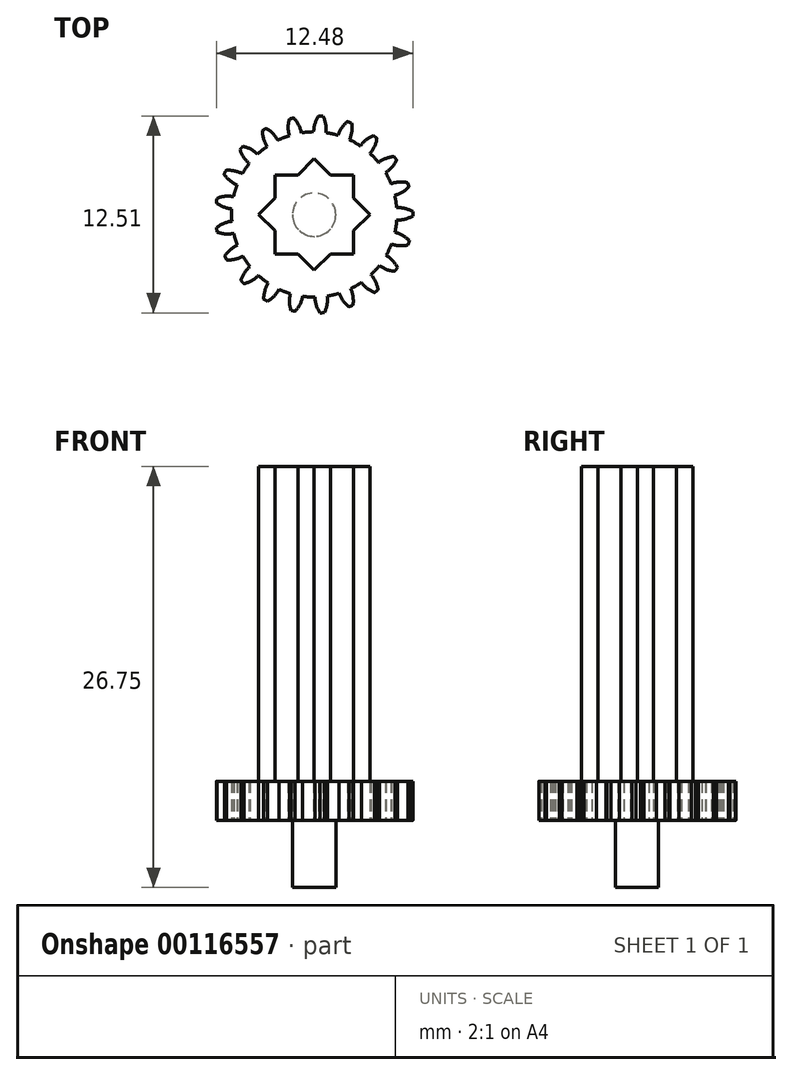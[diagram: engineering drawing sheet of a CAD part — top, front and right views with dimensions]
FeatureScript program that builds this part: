
annotation { "Feature Type Name" : "Feature", "Feature Type Description" : "" }
export const myFeature = defineFeature(function(context is Context, id is Id, definition is map)
    precondition{}
    {
        {
            var Q0;
            Q0=qCreatedBy(makeId("Top.planeOp"),FACE);
            var sketch = newSketch(context, id + "F0", { "sketchPlane" : qUnion([Q0])});
            skLineSegment(sketch, "E0", {"start": v(61.42, 3.14) * mm, "end": v(65.52, 3.14) * mm, "construction": true});
            skLineSegment(sketch, "E1", {"start": v(61.42, 3.14) * mm, "end": v(65.31, 4.4) * mm, "construction": true});
            skLineSegment(sketch, "E2", {"start": v(61.42, 3.14) * mm, "end": v(65.72, 3.82) * mm, "construction": true});
            skPoint(sketch, "E3.third.point", {"position": v(57.79, 0) * mm});
            skArc(sketch, "E4.MirrorCS", {"start": v(62.86, 3.22) * mm, "mid": v(63.38, 3.1) * mm, "end": v(63.92, 3.14) * mm});
            skArc(sketch, "E5.MirrorCS", {"start": v(62.86, 3.22) * mm, "mid": v(62.85, 3.3) * mm, "end": v(62.84, 3.36) * mm});
            skArc(sketch, "E6.MirrorCS", {"start": v(62.82, 3.5) * mm, "mid": v(62.83, 3.43) * mm, "end": v(62.84, 3.36) * mm});
            skArc(sketch, "E7.MirrorCS", {"start": v(62.82, 3.5) * mm, "mid": v(63.28, 3.78) * mm, "end": v(63.8, 3.9) * mm});
            skLineSegment(sketch, "E8", {"start": v(69.03, 4.34) * mm, "end": v(63.8, 3.9) * mm, "construction": true});
            skArc(sketch, "E9.1.0", {"start": v(63.34, 1.7) * mm, "mid": v(63.7, 2.1) * mm, "end": v(64.15, 2.39) * mm});
            skArc(sketch, "E9.1.1", {"start": v(63.34, 1.7) * mm, "mid": v(63.37, 1.64) * mm, "end": v(63.4, 1.58) * mm});
            skArc(sketch, "E9.1.2", {"start": v(63.46, 1.46) * mm, "mid": v(63.43, 1.52) * mm, "end": v(63.4, 1.58) * mm});
            skArc(sketch, "E9.1.3", {"start": v(63.46, 1.46) * mm, "mid": v(64, 1.5) * mm, "end": v(64.5, 1.68) * mm});
            skArc(sketch, "E9.2.0", {"start": v(64.37, 0.15) * mm, "mid": v(64.6, 0.63) * mm, "end": v(64.95, 1.04) * mm});
            skArc(sketch, "E9.2.1", {"start": v(64.37, 0.15) * mm, "mid": v(64.42, 0.1) * mm, "end": v(64.46, 0.05) * mm});
            skArc(sketch, "E9.2.2", {"start": v(64.56, -0.05) * mm, "mid": v(64.51, 0) * mm, "end": v(64.46, 0.05) * mm});
            skArc(sketch, "E9.2.3", {"start": v(64.56, -0.05) * mm, "mid": v(65.06, 0.14) * mm, "end": v(65.48, 0.47) * mm});
            skArc(sketch, "E9.3.0", {"start": v(65.81, -1.04) * mm, "mid": v(65.88, -0.5) * mm, "end": v(66.1, -0.02) * mm});
            skArc(sketch, "E9.3.1", {"start": v(65.81, -1.04) * mm, "mid": v(65.87, -1.07) * mm, "end": v(65.93, -1.1) * mm});
            skArc(sketch, "E9.3.2", {"start": v(66.06, -1.17) * mm, "mid": v(66, -1.14) * mm, "end": v(65.93, -1.1) * mm});
            skArc(sketch, "E9.3.3", {"start": v(66.06, -1.17) * mm, "mid": v(66.47, -0.84) * mm, "end": v(66.78, -0.4) * mm});
            skArc(sketch, "E9.4.0", {"start": v(67.54, -1.74) * mm, "mid": v(67.45, -1.22) * mm, "end": v(67.52, -0.69) * mm});
            skArc(sketch, "E9.4.1", {"start": v(67.54, -1.74) * mm, "mid": v(67.6, -1.76) * mm, "end": v(67.68, -1.78) * mm});
            skArc(sketch, "E9.4.2", {"start": v(67.81, -1.8) * mm, "mid": v(67.75, -1.8) * mm, "end": v(67.68, -1.78) * mm});
            skArc(sketch, "E9.4.3", {"start": v(67.81, -1.8) * mm, "mid": v(68.12, -1.36) * mm, "end": v(68.28, -0.85) * mm});
            skArc(sketch, "E9.5.0", {"start": v(69.4, -1.91) * mm, "mid": v(69.16, -1.43) * mm, "end": v(69.07, -0.9) * mm});
            skArc(sketch, "E9.5.1", {"start": v(69.4, -1.91) * mm, "mid": v(69.47, -1.9) * mm, "end": v(69.54, -1.9) * mm});
            skArc(sketch, "E9.5.2", {"start": v(69.68, -1.89) * mm, "mid": v(69.61, -1.9) * mm, "end": v(69.54, -1.9) * mm});
            skArc(sketch, "E9.5.3", {"start": v(69.68, -1.89) * mm, "mid": v(69.84, -1.38) * mm, "end": v(69.85, -0.84) * mm});
            skArc(sketch, "E9.6.0", {"start": v(71.23, -1.52) * mm, "mid": v(70.86, -1.14) * mm, "end": v(70.61, -0.66) * mm});
            skArc(sketch, "E9.6.1", {"start": v(71.23, -1.52) * mm, "mid": v(71.3, -1.5) * mm, "end": v(71.36, -1.47) * mm});
            skArc(sketch, "E9.6.2", {"start": v(71.49, -1.42) * mm, "mid": v(71.42, -1.45) * mm, "end": v(71.36, -1.47) * mm});
            skArc(sketch, "E9.6.3", {"start": v(71.49, -1.42) * mm, "mid": v(71.49, -0.88) * mm, "end": v(71.34, -0.37) * mm});
            skArc(sketch, "E9.7.0", {"start": v(72.86, -0.61) * mm, "mid": v(72.4, -0.35) * mm, "end": v(72.02, 0.03) * mm});
            skArc(sketch, "E9.7.1", {"start": v(72.86, -0.61) * mm, "mid": v(72.91, -0.57) * mm, "end": v(72.97, -0.53) * mm});
            skArc(sketch, "E9.7.2", {"start": v(73.08, -0.44) * mm, "mid": v(73.02, -0.48) * mm, "end": v(72.97, -0.53) * mm});
            skArc(sketch, "E9.7.3", {"start": v(73.08, -0.44) * mm, "mid": v(72.92, 0.07) * mm, "end": v(72.62, 0.52) * mm});
            skArc(sketch, "E9.8.0", {"start": v(74.15, 0.74) * mm, "mid": v(73.63, 0.85) * mm, "end": v(73.16, 1.1) * mm});
            skArc(sketch, "E9.8.1", {"start": v(74.15, 0.74) * mm, "mid": v(74.19, 0.8) * mm, "end": v(74.23, 0.85) * mm});
            skArc(sketch, "E9.8.2", {"start": v(74.3, 0.97) * mm, "mid": v(74.27, 0.9) * mm, "end": v(74.23, 0.85) * mm});
            skArc(sketch, "E9.8.3", {"start": v(74.3, 0.97) * mm, "mid": v(74, 1.41) * mm, "end": v(73.6, 1.75) * mm});
            skArc(sketch, "E9.9.0", {"start": v(74.98, 2.4) * mm, "mid": v(74.45, 2.36) * mm, "end": v(73.93, 2.46) * mm});
            skArc(sketch, "E9.9.1", {"start": v(74.98, 2.4) * mm, "mid": v(75, 2.47) * mm, "end": v(75.03, 2.54) * mm});
            skArc(sketch, "E9.9.2", {"start": v(75.06, 2.67) * mm, "mid": v(75.05, 2.6) * mm, "end": v(75.03, 2.54) * mm});
            skArc(sketch, "E9.9.3", {"start": v(75.06, 2.67) * mm, "mid": v(74.65, 3) * mm, "end": v(74.15, 3.21) * mm});
            skArc(sketch, "E9.10.0", {"start": v(75.29, 4.25) * mm, "mid": v(74.8, 4.05) * mm, "end": v(74.26, 4) * mm});
            skArc(sketch, "E9.10.1", {"start": v(75.29, 4.25) * mm, "mid": v(75.3, 4.32) * mm, "end": v(75.3, 4.39) * mm});
            skArc(sketch, "E9.10.2", {"start": v(75.29, 4.53) * mm, "mid": v(75.3, 4.46) * mm, "end": v(75.3, 4.39) * mm});
            skArc(sketch, "E9.10.3", {"start": v(75.29, 4.53) * mm, "mid": v(74.8, 4.72) * mm, "end": v(74.26, 4.77) * mm});
            skArc(sketch, "E9.11.0", {"start": v(75.04, 6.1) * mm, "mid": v(74.63, 5.76) * mm, "end": v(74.13, 5.55) * mm});
            skArc(sketch, "E9.11.1", {"start": v(75.04, 6.1) * mm, "mid": v(75.02, 6.17) * mm, "end": v(75, 6.23) * mm});
            skArc(sketch, "E9.11.2", {"start": v(74.95, 6.37) * mm, "mid": v(74.98, 6.3) * mm, "end": v(75, 6.23) * mm});
            skArc(sketch, "E9.11.3", {"start": v(74.95, 6.37) * mm, "mid": v(74.42, 6.4) * mm, "end": v(73.9, 6.3) * mm});
            skArc(sketch, "E9.12.0", {"start": v(74.25, 7.8) * mm, "mid": v(73.96, 7.35) * mm, "end": v(73.55, 7) * mm});
            skArc(sketch, "E9.12.1", {"start": v(74.25, 7.8) * mm, "mid": v(74.22, 7.85) * mm, "end": v(74.18, 7.91) * mm});
            skArc(sketch, "E9.12.2", {"start": v(74.1, 8.02) * mm, "mid": v(74.14, 7.97) * mm, "end": v(74.18, 7.91) * mm});
            skArc(sketch, "E9.12.3", {"start": v(74.1, 8.02) * mm, "mid": v(73.57, 7.9) * mm, "end": v(73.1, 7.65) * mm});
            skArc(sketch, "E9.13.0", {"start": v(73, 9.18) * mm, "mid": v(72.85, 8.67) * mm, "end": v(72.57, 8.22) * mm});
            skArc(sketch, "E9.13.1", {"start": v(73, 9.18) * mm, "mid": v(72.95, 9.23) * mm, "end": v(72.9, 9.27) * mm});
            skArc(sketch, "E9.13.2", {"start": v(72.78, 9.35) * mm, "mid": v(72.84, 9.31) * mm, "end": v(72.9, 9.27) * mm});
            skArc(sketch, "E9.13.3", {"start": v(72.78, 9.35) * mm, "mid": v(72.32, 9.09) * mm, "end": v(71.95, 8.7) * mm});
            skArc(sketch, "E9.14.0", {"start": v(71.4, 10.14) * mm, "mid": v(71.4, 9.6) * mm, "end": v(71.27, 9.09) * mm});
            skArc(sketch, "E9.14.1", {"start": v(71.4, 10.14) * mm, "mid": v(71.34, 10.17) * mm, "end": v(71.27, 10.2) * mm});
            skArc(sketch, "E9.14.2", {"start": v(71.14, 10.24) * mm, "mid": v(71.2, 10.22) * mm, "end": v(71.27, 10.2) * mm});
            skArc(sketch, "E9.14.3", {"start": v(71.14, 10.24) * mm, "mid": v(70.78, 9.85) * mm, "end": v(70.54, 9.37) * mm});
            skArc(sketch, "E9.15.0", {"start": v(69.59, 10.58) * mm, "mid": v(69.75, 10.07) * mm, "end": v(69.77, 9.54) * mm});
            skArc(sketch, "E9.15.1", {"start": v(69.59, 10.58) * mm, "mid": v(69.52, 10.59) * mm, "end": v(69.45, 10.6) * mm});
            skArc(sketch, "E9.15.2", {"start": v(69.3, 10.6) * mm, "mid": v(69.38, 10.6) * mm, "end": v(69.45, 10.6) * mm});
            skArc(sketch, "E9.15.3", {"start": v(69.3, 10.6) * mm, "mid": v(69.07, 10.12) * mm, "end": v(68.99, 9.6) * mm});
            skArc(sketch, "E9.16.0", {"start": v(67.72, 10.47) * mm, "mid": v(68.03, 10.03) * mm, "end": v(68.2, 9.53) * mm});
            skArc(sketch, "E9.16.1", {"start": v(67.72, 10.47) * mm, "mid": v(67.65, 10.46) * mm, "end": v(67.59, 10.44) * mm});
            skArc(sketch, "E9.16.2", {"start": v(67.45, 10.4) * mm, "mid": v(67.52, 10.42) * mm, "end": v(67.59, 10.44) * mm});
            skArc(sketch, "E9.16.3", {"start": v(67.45, 10.4) * mm, "mid": v(67.37, 9.88) * mm, "end": v(67.44, 9.35) * mm});
            skArc(sketch, "E9.17.0", {"start": v(65.97, 9.81) * mm, "mid": v(66.4, 9.49) * mm, "end": v(66.71, 9.05) * mm});
            skArc(sketch, "E9.17.1", {"start": v(65.97, 9.81) * mm, "mid": v(65.91, 9.78) * mm, "end": v(65.85, 9.75) * mm});
            skArc(sketch, "E9.17.2", {"start": v(65.73, 9.67) * mm, "mid": v(65.8, 9.7) * mm, "end": v(65.85, 9.75) * mm});
            skArc(sketch, "E9.17.3", {"start": v(65.73, 9.67) * mm, "mid": v(65.81, 9.14) * mm, "end": v(66.04, 8.66) * mm});
            skArc(sketch, "E9.18.0", {"start": v(64.5, 8.67) * mm, "mid": v(65, 8.48) * mm, "end": v(65.43, 8.16) * mm});
            skArc(sketch, "E9.18.1", {"start": v(64.5, 8.67) * mm, "mid": v(64.45, 8.62) * mm, "end": v(64.4, 8.57) * mm});
            skArc(sketch, "E9.18.2", {"start": v(64.3, 8.47) * mm, "mid": v(64.35, 8.52) * mm, "end": v(64.4, 8.57) * mm});
            skArc(sketch, "E9.18.3", {"start": v(64.3, 8.47) * mm, "mid": v(64.54, 7.98) * mm, "end": v(64.9, 7.59) * mm});
            skArc(sketch, "E9.19.0", {"start": v(63.42, 7.14) * mm, "mid": v(63.96, 7.11) * mm, "end": v(64.46, 6.93) * mm});
            skArc(sketch, "E9.19.1", {"start": v(63.42, 7.14) * mm, "mid": v(63.4, 7.08) * mm, "end": v(63.36, 7.02) * mm});
            skArc(sketch, "E9.19.2", {"start": v(63.3, 6.9) * mm, "mid": v(63.33, 6.96) * mm, "end": v(63.36, 7.02) * mm});
            skArc(sketch, "E9.19.3", {"start": v(63.3, 6.9) * mm, "mid": v(63.67, 6.5) * mm, "end": v(64.12, 6.22) * mm});
            skArc(sketch, "E9.20.0", {"start": v(62.85, 5.37) * mm, "mid": v(63.36, 5.5) * mm, "end": v(63.9, 5.47) * mm});
            skArc(sketch, "E9.20.1", {"start": v(62.85, 5.37) * mm, "mid": v(62.83, 5.3) * mm, "end": v(62.82, 5.23) * mm});
            skArc(sketch, "E9.20.2", {"start": v(62.8, 5.1) * mm, "mid": v(62.81, 5.16) * mm, "end": v(62.82, 5.23) * mm});
            skArc(sketch, "E9.20.3", {"start": v(62.8, 5.1) * mm, "mid": v(63.27, 4.82) * mm, "end": v(63.79, 4.7) * mm});
            skPoint(sketch, "E9.center", {"position": v(69.03, 4.34) * mm});
            skCircle(sketch, "E10", {"center": v(69.03, 4.34) * mm, "radius": 5.25 * mm});
            skSolve(sketch);
        }
        {
            var Q0;
            Q0=qSketchRegion(id+"F0",true);
            extrude(context, id + "F1", {"entities" : qUnion([Q0]), "depth" : 2.5 * mm});
        }
        {
            var Q0;
            Q0=makeQuery(id+"F1.opExtrude","CAP_FACE",FACE,{"disambiguationData":[OSD([sQuery(id+"F0.wireOp",EDGE,"E4.MirrorCS"),sQuery(id+"F0.wireOp",EDGE,"E5.MirrorCS"),sQuery(id+"F0.wireOp",EDGE,"E6.MirrorCS"),sQuery(id+"F0.wireOp",EDGE,"E7.MirrorCS"),sQuery(id+"F0.wireOp",EDGE,"3aad1c11-f46f-48f3-83f1-c81cc0587eb40.MirrorCS"),sQuery(id+"F0.wireOp",EDGE,"261d038e-785b-489d-9701-d77bc27e36f7.1.0"),sQuery(id+"F0.wireOp",EDGE,"261d038e-785b-489d-9701-d77bc27e36f7.1.1"),sQuery(id+"F0.wireOp",EDGE,"261d038e-785b-489d-9701-d77bc27e36f7.1.2"),sQuery(id+"F0.wireOp",EDGE,"261d038e-785b-489d-9701-d77bc27e36f7.1.3"),sQuery(id+"F0.wireOp",EDGE,"261d038e-785b-489d-9701-d77bc27e36f7.1.4"),sQuery(id+"F0.wireOp",EDGE,"261d038e-785b-489d-9701-d77bc27e36f7.2.0"),sQuery(id+"F0.wireOp",EDGE,"261d038e-785b-489d-9701-d77bc27e36f7.2.1"),sQuery(id+"F0.wireOp",EDGE,"261d038e-785b-489d-9701-d77bc27e36f7.2.2"),sQuery(id+"F0.wireOp",EDGE,"261d038e-785b-489d-9701-d77bc27e36f7.2.3"),sQuery(id+"F0.wireOp",EDGE,"261d038e-785b-489d-9701-d77bc27e36f7.2.4"),sQuery(id+"F0.wireOp",EDGE,"261d038e-785b-489d-9701-d77bc27e36f7.3.0"),sQuery(id+"F0.wireOp",EDGE,"261d038e-785b-489d-9701-d77bc27e36f7.3.1"),sQuery(id+"F0.wireOp",EDGE,"261d038e-785b-489d-9701-d77bc27e36f7.3.2"),sQuery(id+"F0.wireOp",EDGE,"261d038e-785b-489d-9701-d77bc27e36f7.3.3"),sQuery(id+"F0.wireOp",EDGE,"261d038e-785b-489d-9701-d77bc27e36f7.3.4"),sQuery(id+"F0.wireOp",EDGE,"261d038e-785b-489d-9701-d77bc27e36f7.4.0"),sQuery(id+"F0.wireOp",EDGE,"261d038e-785b-489d-9701-d77bc27e36f7.4.1"),sQuery(id+"F0.wireOp",EDGE,"261d038e-785b-489d-9701-d77bc27e36f7.4.2"),sQuery(id+"F0.wireOp",EDGE,"261d038e-785b-489d-9701-d77bc27e36f7.4.3"),sQuery(id+"F0.wireOp",EDGE,"261d038e-785b-489d-9701-d77bc27e36f7.4.4"),sQuery(id+"F0.wireOp",EDGE,"261d038e-785b-489d-9701-d77bc27e36f7.5.0"),sQuery(id+"F0.wireOp",EDGE,"261d038e-785b-489d-9701-d77bc27e36f7.5.1"),sQuery(id+"F0.wireOp",EDGE,"261d038e-785b-489d-9701-d77bc27e36f7.5.2"),sQuery(id+"F0.wireOp",EDGE,"261d038e-785b-489d-9701-d77bc27e36f7.5.3"),sQuery(id+"F0.wireOp",EDGE,"261d038e-785b-489d-9701-d77bc27e36f7.5.4"),sQuery(id+"F0.wireOp",EDGE,"261d038e-785b-489d-9701-d77bc27e36f7.6.0"),sQuery(id+"F0.wireOp",EDGE,"261d038e-785b-489d-9701-d77bc27e36f7.6.1"),sQuery(id+"F0.wireOp",EDGE,"261d038e-785b-489d-9701-d77bc27e36f7.6.2"),sQuery(id+"F0.wireOp",EDGE,"261d038e-785b-489d-9701-d77bc27e36f7.6.3"),sQuery(id+"F0.wireOp",EDGE,"261d038e-785b-489d-9701-d77bc27e36f7.6.4"),sQuery(id+"F0.wireOp",EDGE,"261d038e-785b-489d-9701-d77bc27e36f7.7.0"),sQuery(id+"F0.wireOp",EDGE,"261d038e-785b-489d-9701-d77bc27e36f7.7.1"),sQuery(id+"F0.wireOp",EDGE,"261d038e-785b-489d-9701-d77bc27e36f7.7.2"),sQuery(id+"F0.wireOp",EDGE,"261d038e-785b-489d-9701-d77bc27e36f7.7.3"),sQuery(id+"F0.wireOp",EDGE,"261d038e-785b-489d-9701-d77bc27e36f7.7.4"),sQuery(id+"F0.wireOp",EDGE,"261d038e-785b-489d-9701-d77bc27e36f7.8.0"),sQuery(id+"F0.wireOp",EDGE,"261d038e-785b-489d-9701-d77bc27e36f7.8.1"),sQuery(id+"F0.wireOp",EDGE,"261d038e-785b-489d-9701-d77bc27e36f7.8.2"),sQuery(id+"F0.wireOp",EDGE,"261d038e-785b-489d-9701-d77bc27e36f7.8.3"),sQuery(id+"F0.wireOp",EDGE,"261d038e-785b-489d-9701-d77bc27e36f7.8.4"),sQuery(id+"F0.wireOp",EDGE,"261d038e-785b-489d-9701-d77bc27e36f7.9.0"),sQuery(id+"F0.wireOp",EDGE,"261d038e-785b-489d-9701-d77bc27e36f7.9.1"),sQuery(id+"F0.wireOp",EDGE,"261d038e-785b-489d-9701-d77bc27e36f7.9.2"),sQuery(id+"F0.wireOp",EDGE,"261d038e-785b-489d-9701-d77bc27e36f7.9.3"),sQuery(id+"F0.wireOp",EDGE,"261d038e-785b-489d-9701-d77bc27e36f7.9.4"),sQuery(id+"F0.wireOp",EDGE,"261d038e-785b-489d-9701-d77bc27e36f7.10.0"),sQuery(id+"F0.wireOp",EDGE,"261d038e-785b-489d-9701-d77bc27e36f7.10.1"),sQuery(id+"F0.wireOp",EDGE,"261d038e-785b-489d-9701-d77bc27e36f7.10.2"),sQuery(id+"F0.wireOp",EDGE,"261d038e-785b-489d-9701-d77bc27e36f7.10.3"),sQuery(id+"F0.wireOp",EDGE,"261d038e-785b-489d-9701-d77bc27e36f7.10.4"),sQuery(id+"F0.wireOp",EDGE,"261d038e-785b-489d-9701-d77bc27e36f7.11.0"),sQuery(id+"F0.wireOp",EDGE,"261d038e-785b-489d-9701-d77bc27e36f7.11.1"),sQuery(id+"F0.wireOp",EDGE,"261d038e-785b-489d-9701-d77bc27e36f7.11.2"),sQuery(id+"F0.wireOp",EDGE,"261d038e-785b-489d-9701-d77bc27e36f7.11.3"),sQuery(id+"F0.wireOp",EDGE,"261d038e-785b-489d-9701-d77bc27e36f7.11.4"),sQuery(id+"F0.wireOp",EDGE,"261d038e-785b-489d-9701-d77bc27e36f7.12.0"),sQuery(id+"F0.wireOp",EDGE,"261d038e-785b-489d-9701-d77bc27e36f7.12.1"),sQuery(id+"F0.wireOp",EDGE,"261d038e-785b-489d-9701-d77bc27e36f7.12.2"),sQuery(id+"F0.wireOp",EDGE,"261d038e-785b-489d-9701-d77bc27e36f7.12.3"),sQuery(id+"F0.wireOp",EDGE,"261d038e-785b-489d-9701-d77bc27e36f7.12.4"),sQuery(id+"F0.wireOp",EDGE,"261d038e-785b-489d-9701-d77bc27e36f7.13.0"),sQuery(id+"F0.wireOp",EDGE,"261d038e-785b-489d-9701-d77bc27e36f7.13.1"),sQuery(id+"F0.wireOp",EDGE,"261d038e-785b-489d-9701-d77bc27e36f7.13.2"),sQuery(id+"F0.wireOp",EDGE,"261d038e-785b-489d-9701-d77bc27e36f7.13.3"),sQuery(id+"F0.wireOp",EDGE,"261d038e-785b-489d-9701-d77bc27e36f7.13.4"),sQuery(id+"F0.wireOp",EDGE,"261d038e-785b-489d-9701-d77bc27e36f7.14.0"),sQuery(id+"F0.wireOp",EDGE,"261d038e-785b-489d-9701-d77bc27e36f7.14.1"),sQuery(id+"F0.wireOp",EDGE,"261d038e-785b-489d-9701-d77bc27e36f7.14.2"),sQuery(id+"F0.wireOp",EDGE,"261d038e-785b-489d-9701-d77bc27e36f7.14.3"),sQuery(id+"F0.wireOp",EDGE,"261d038e-785b-489d-9701-d77bc27e36f7.14.4"),sQuery(id+"F0.wireOp",EDGE,"261d038e-785b-489d-9701-d77bc27e36f7.15.0"),sQuery(id+"F0.wireOp",EDGE,"261d038e-785b-489d-9701-d77bc27e36f7.15.1"),sQuery(id+"F0.wireOp",EDGE,"261d038e-785b-489d-9701-d77bc27e36f7.15.2"),sQuery(id+"F0.wireOp",EDGE,"261d038e-785b-489d-9701-d77bc27e36f7.15.3"),sQuery(id+"F0.wireOp",EDGE,"261d038e-785b-489d-9701-d77bc27e36f7.15.4"),sQuery(id+"F0.wireOp",EDGE,"261d038e-785b-489d-9701-d77bc27e36f7.16.0"),sQuery(id+"F0.wireOp",EDGE,"261d038e-785b-489d-9701-d77bc27e36f7.16.1"),sQuery(id+"F0.wireOp",EDGE,"261d038e-785b-489d-9701-d77bc27e36f7.16.2"),sQuery(id+"F0.wireOp",EDGE,"261d038e-785b-489d-9701-d77bc27e36f7.16.3"),sQuery(id+"F0.wireOp",EDGE,"261d038e-785b-489d-9701-d77bc27e36f7.16.4"),sQuery(id+"F0.wireOp",EDGE,"261d038e-785b-489d-9701-d77bc27e36f7.17.0"),sQuery(id+"F0.wireOp",EDGE,"261d038e-785b-489d-9701-d77bc27e36f7.17.1"),sQuery(id+"F0.wireOp",EDGE,"261d038e-785b-489d-9701-d77bc27e36f7.17.2"),sQuery(id+"F0.wireOp",EDGE,"261d038e-785b-489d-9701-d77bc27e36f7.17.3"),sQuery(id+"F0.wireOp",EDGE,"261d038e-785b-489d-9701-d77bc27e36f7.17.4"),sQuery(id+"F0.wireOp",EDGE,"261d038e-785b-489d-9701-d77bc27e36f7.18.0"),sQuery(id+"F0.wireOp",EDGE,"261d038e-785b-489d-9701-d77bc27e36f7.18.1"),sQuery(id+"F0.wireOp",EDGE,"261d038e-785b-489d-9701-d77bc27e36f7.18.2"),sQuery(id+"F0.wireOp",EDGE,"261d038e-785b-489d-9701-d77bc27e36f7.18.3"),sQuery(id+"F0.wireOp",EDGE,"261d038e-785b-489d-9701-d77bc27e36f7.18.4"),sQuery(id+"F0.wireOp",EDGE,"261d038e-785b-489d-9701-d77bc27e36f7.19.0"),sQuery(id+"F0.wireOp",EDGE,"261d038e-785b-489d-9701-d77bc27e36f7.19.1"),sQuery(id+"F0.wireOp",EDGE,"261d038e-785b-489d-9701-d77bc27e36f7.19.2"),sQuery(id+"F0.wireOp",EDGE,"261d038e-785b-489d-9701-d77bc27e36f7.19.3"),sQuery(id+"F0.wireOp",EDGE,"261d038e-785b-489d-9701-d77bc27e36f7.19.4"),sQuery(id+"F0.wireOp",EDGE,"f45ad2ee-8b84-45a9-bb91-348b52f7b137.4.20.0"),sQuery(id+"F0.wireOp",EDGE,"f45ad2ee-8b84-45a9-bb91-348b52f7b137.8.20.0"),sQuery(id+"F0.wireOp",EDGE,"f45ad2ee-8b84-45a9-bb91-348b52f7b137.12.20.0"),sQuery(id+"F0.wireOp",EDGE,"f45ad2ee-8b84-45a9-bb91-348b52f7b137.15.20.0"),sQuery(id+"F0.wireOp",EDGE,"f45ad2ee-8b84-45a9-bb91-348b52f7b137.16.20.0")])],"isStart":false});
            var sketch = newSketch(context, id + "F2", { "sketchPlane" : qUnion([Q0])});
            skLineSegment(sketch, "E11.bottom", {"start": v(71.53, 1.84) * mm, "end": v(66.53, 1.84) * mm});
            skLineSegment(sketch, "E11.top", {"start": v(71.53, 6.84) * mm, "end": v(66.53, 6.84) * mm});
            skLineSegment(sketch, "E11.left", {"start": v(71.53, 1.84) * mm, "end": v(71.53, 6.84) * mm});
            skLineSegment(sketch, "E11.right", {"start": v(66.53, 1.84) * mm, "end": v(66.53, 6.84) * mm});
            skPoint(sketch, "E11.middle", {"position": v(69.03, 4.34) * mm});
            skLineSegment(sketch, "E12", {"start": v(65.5, 4.34) * mm, "end": v(69.03, 7.88) * mm});
            skLineSegment(sketch, "E13", {"start": v(69.03, 7.88) * mm, "end": v(72.56, 4.34) * mm});
            skLineSegment(sketch, "E14", {"start": v(72.56, 4.34) * mm, "end": v(69.03, 0.8) * mm});
            skLineSegment(sketch, "E15", {"start": v(69.03, 0.8) * mm, "end": v(65.5, 4.34) * mm});
            skLineSegment(sketch, "E16", {"start": v(68.6, 9.57) * mm, "end": v(69.54, -1.9) * mm, "construction": true});
            skLineSegment(sketch, "E17", {"start": v(64, 5.85) * mm, "end": v(75.03, 2.54) * mm, "construction": true});
            skSolve(sketch);
        }
        {
            var Q0;
            Q0=qSketchRegion(id+"F2",true);
            extrude(context, id + "F3", {"entities" : qUnion([Q0]), "operationType" : NewBodyOperationType.ADD, "depth" : 20 * mm});
        }
        {
            var Q0;
            Q0=makeQuery(id+"F1.opExtrude","CAP_FACE",FACE,{"disambiguationData":[OSD([sQuery(id+"F0.wireOp",EDGE,"E4.MirrorCS"),sQuery(id+"F0.wireOp",EDGE,"E5.MirrorCS"),sQuery(id+"F0.wireOp",EDGE,"E6.MirrorCS"),sQuery(id+"F0.wireOp",EDGE,"E7.MirrorCS"),sQuery(id+"F0.wireOp",EDGE,"3aad1c11-f46f-48f3-83f1-c81cc0587eb40.MirrorCS"),sQuery(id+"F0.wireOp",EDGE,"261d038e-785b-489d-9701-d77bc27e36f7.1.0"),sQuery(id+"F0.wireOp",EDGE,"261d038e-785b-489d-9701-d77bc27e36f7.1.1"),sQuery(id+"F0.wireOp",EDGE,"261d038e-785b-489d-9701-d77bc27e36f7.1.2"),sQuery(id+"F0.wireOp",EDGE,"261d038e-785b-489d-9701-d77bc27e36f7.1.3"),sQuery(id+"F0.wireOp",EDGE,"261d038e-785b-489d-9701-d77bc27e36f7.1.4"),sQuery(id+"F0.wireOp",EDGE,"261d038e-785b-489d-9701-d77bc27e36f7.2.0"),sQuery(id+"F0.wireOp",EDGE,"261d038e-785b-489d-9701-d77bc27e36f7.2.1"),sQuery(id+"F0.wireOp",EDGE,"261d038e-785b-489d-9701-d77bc27e36f7.2.2"),sQuery(id+"F0.wireOp",EDGE,"261d038e-785b-489d-9701-d77bc27e36f7.2.3"),sQuery(id+"F0.wireOp",EDGE,"261d038e-785b-489d-9701-d77bc27e36f7.2.4"),sQuery(id+"F0.wireOp",EDGE,"261d038e-785b-489d-9701-d77bc27e36f7.3.0"),sQuery(id+"F0.wireOp",EDGE,"261d038e-785b-489d-9701-d77bc27e36f7.3.1"),sQuery(id+"F0.wireOp",EDGE,"261d038e-785b-489d-9701-d77bc27e36f7.3.2"),sQuery(id+"F0.wireOp",EDGE,"261d038e-785b-489d-9701-d77bc27e36f7.3.3"),sQuery(id+"F0.wireOp",EDGE,"261d038e-785b-489d-9701-d77bc27e36f7.3.4"),sQuery(id+"F0.wireOp",EDGE,"261d038e-785b-489d-9701-d77bc27e36f7.4.0"),sQuery(id+"F0.wireOp",EDGE,"261d038e-785b-489d-9701-d77bc27e36f7.4.1"),sQuery(id+"F0.wireOp",EDGE,"261d038e-785b-489d-9701-d77bc27e36f7.4.2"),sQuery(id+"F0.wireOp",EDGE,"261d038e-785b-489d-9701-d77bc27e36f7.4.3"),sQuery(id+"F0.wireOp",EDGE,"261d038e-785b-489d-9701-d77bc27e36f7.4.4"),sQuery(id+"F0.wireOp",EDGE,"261d038e-785b-489d-9701-d77bc27e36f7.5.0"),sQuery(id+"F0.wireOp",EDGE,"261d038e-785b-489d-9701-d77bc27e36f7.5.1"),sQuery(id+"F0.wireOp",EDGE,"261d038e-785b-489d-9701-d77bc27e36f7.5.2"),sQuery(id+"F0.wireOp",EDGE,"261d038e-785b-489d-9701-d77bc27e36f7.5.3"),sQuery(id+"F0.wireOp",EDGE,"261d038e-785b-489d-9701-d77bc27e36f7.5.4"),sQuery(id+"F0.wireOp",EDGE,"261d038e-785b-489d-9701-d77bc27e36f7.6.0"),sQuery(id+"F0.wireOp",EDGE,"261d038e-785b-489d-9701-d77bc27e36f7.6.1"),sQuery(id+"F0.wireOp",EDGE,"261d038e-785b-489d-9701-d77bc27e36f7.6.2"),sQuery(id+"F0.wireOp",EDGE,"261d038e-785b-489d-9701-d77bc27e36f7.6.3"),sQuery(id+"F0.wireOp",EDGE,"261d038e-785b-489d-9701-d77bc27e36f7.6.4"),sQuery(id+"F0.wireOp",EDGE,"261d038e-785b-489d-9701-d77bc27e36f7.7.0"),sQuery(id+"F0.wireOp",EDGE,"261d038e-785b-489d-9701-d77bc27e36f7.7.1"),sQuery(id+"F0.wireOp",EDGE,"261d038e-785b-489d-9701-d77bc27e36f7.7.2"),sQuery(id+"F0.wireOp",EDGE,"261d038e-785b-489d-9701-d77bc27e36f7.7.3"),sQuery(id+"F0.wireOp",EDGE,"261d038e-785b-489d-9701-d77bc27e36f7.7.4"),sQuery(id+"F0.wireOp",EDGE,"261d038e-785b-489d-9701-d77bc27e36f7.8.0"),sQuery(id+"F0.wireOp",EDGE,"261d038e-785b-489d-9701-d77bc27e36f7.8.1"),sQuery(id+"F0.wireOp",EDGE,"261d038e-785b-489d-9701-d77bc27e36f7.8.2"),sQuery(id+"F0.wireOp",EDGE,"261d038e-785b-489d-9701-d77bc27e36f7.8.3"),sQuery(id+"F0.wireOp",EDGE,"261d038e-785b-489d-9701-d77bc27e36f7.8.4"),sQuery(id+"F0.wireOp",EDGE,"261d038e-785b-489d-9701-d77bc27e36f7.9.0"),sQuery(id+"F0.wireOp",EDGE,"261d038e-785b-489d-9701-d77bc27e36f7.9.1"),sQuery(id+"F0.wireOp",EDGE,"261d038e-785b-489d-9701-d77bc27e36f7.9.2"),sQuery(id+"F0.wireOp",EDGE,"261d038e-785b-489d-9701-d77bc27e36f7.9.3"),sQuery(id+"F0.wireOp",EDGE,"261d038e-785b-489d-9701-d77bc27e36f7.9.4"),sQuery(id+"F0.wireOp",EDGE,"261d038e-785b-489d-9701-d77bc27e36f7.10.0"),sQuery(id+"F0.wireOp",EDGE,"261d038e-785b-489d-9701-d77bc27e36f7.10.1"),sQuery(id+"F0.wireOp",EDGE,"261d038e-785b-489d-9701-d77bc27e36f7.10.2"),sQuery(id+"F0.wireOp",EDGE,"261d038e-785b-489d-9701-d77bc27e36f7.10.3"),sQuery(id+"F0.wireOp",EDGE,"261d038e-785b-489d-9701-d77bc27e36f7.10.4"),sQuery(id+"F0.wireOp",EDGE,"261d038e-785b-489d-9701-d77bc27e36f7.11.0"),sQuery(id+"F0.wireOp",EDGE,"261d038e-785b-489d-9701-d77bc27e36f7.11.1"),sQuery(id+"F0.wireOp",EDGE,"261d038e-785b-489d-9701-d77bc27e36f7.11.2"),sQuery(id+"F0.wireOp",EDGE,"261d038e-785b-489d-9701-d77bc27e36f7.11.3"),sQuery(id+"F0.wireOp",EDGE,"261d038e-785b-489d-9701-d77bc27e36f7.11.4"),sQuery(id+"F0.wireOp",EDGE,"261d038e-785b-489d-9701-d77bc27e36f7.12.0"),sQuery(id+"F0.wireOp",EDGE,"261d038e-785b-489d-9701-d77bc27e36f7.12.1"),sQuery(id+"F0.wireOp",EDGE,"261d038e-785b-489d-9701-d77bc27e36f7.12.2"),sQuery(id+"F0.wireOp",EDGE,"261d038e-785b-489d-9701-d77bc27e36f7.12.3"),sQuery(id+"F0.wireOp",EDGE,"261d038e-785b-489d-9701-d77bc27e36f7.12.4"),sQuery(id+"F0.wireOp",EDGE,"261d038e-785b-489d-9701-d77bc27e36f7.13.0"),sQuery(id+"F0.wireOp",EDGE,"261d038e-785b-489d-9701-d77bc27e36f7.13.1"),sQuery(id+"F0.wireOp",EDGE,"261d038e-785b-489d-9701-d77bc27e36f7.13.2"),sQuery(id+"F0.wireOp",EDGE,"261d038e-785b-489d-9701-d77bc27e36f7.13.3"),sQuery(id+"F0.wireOp",EDGE,"261d038e-785b-489d-9701-d77bc27e36f7.13.4"),sQuery(id+"F0.wireOp",EDGE,"261d038e-785b-489d-9701-d77bc27e36f7.14.0"),sQuery(id+"F0.wireOp",EDGE,"261d038e-785b-489d-9701-d77bc27e36f7.14.1"),sQuery(id+"F0.wireOp",EDGE,"261d038e-785b-489d-9701-d77bc27e36f7.14.2"),sQuery(id+"F0.wireOp",EDGE,"261d038e-785b-489d-9701-d77bc27e36f7.14.3"),sQuery(id+"F0.wireOp",EDGE,"261d038e-785b-489d-9701-d77bc27e36f7.14.4"),sQuery(id+"F0.wireOp",EDGE,"261d038e-785b-489d-9701-d77bc27e36f7.15.0"),sQuery(id+"F0.wireOp",EDGE,"261d038e-785b-489d-9701-d77bc27e36f7.15.1"),sQuery(id+"F0.wireOp",EDGE,"261d038e-785b-489d-9701-d77bc27e36f7.15.2"),sQuery(id+"F0.wireOp",EDGE,"261d038e-785b-489d-9701-d77bc27e36f7.15.3"),sQuery(id+"F0.wireOp",EDGE,"261d038e-785b-489d-9701-d77bc27e36f7.15.4"),sQuery(id+"F0.wireOp",EDGE,"261d038e-785b-489d-9701-d77bc27e36f7.16.0"),sQuery(id+"F0.wireOp",EDGE,"261d038e-785b-489d-9701-d77bc27e36f7.16.1"),sQuery(id+"F0.wireOp",EDGE,"261d038e-785b-489d-9701-d77bc27e36f7.16.2"),sQuery(id+"F0.wireOp",EDGE,"261d038e-785b-489d-9701-d77bc27e36f7.16.3"),sQuery(id+"F0.wireOp",EDGE,"261d038e-785b-489d-9701-d77bc27e36f7.16.4"),sQuery(id+"F0.wireOp",EDGE,"261d038e-785b-489d-9701-d77bc27e36f7.17.0"),sQuery(id+"F0.wireOp",EDGE,"261d038e-785b-489d-9701-d77bc27e36f7.17.1"),sQuery(id+"F0.wireOp",EDGE,"261d038e-785b-489d-9701-d77bc27e36f7.17.2"),sQuery(id+"F0.wireOp",EDGE,"261d038e-785b-489d-9701-d77bc27e36f7.17.3"),sQuery(id+"F0.wireOp",EDGE,"261d038e-785b-489d-9701-d77bc27e36f7.17.4"),sQuery(id+"F0.wireOp",EDGE,"261d038e-785b-489d-9701-d77bc27e36f7.18.0"),sQuery(id+"F0.wireOp",EDGE,"261d038e-785b-489d-9701-d77bc27e36f7.18.1"),sQuery(id+"F0.wireOp",EDGE,"261d038e-785b-489d-9701-d77bc27e36f7.18.2"),sQuery(id+"F0.wireOp",EDGE,"261d038e-785b-489d-9701-d77bc27e36f7.18.3"),sQuery(id+"F0.wireOp",EDGE,"261d038e-785b-489d-9701-d77bc27e36f7.18.4"),sQuery(id+"F0.wireOp",EDGE,"261d038e-785b-489d-9701-d77bc27e36f7.19.0"),sQuery(id+"F0.wireOp",EDGE,"261d038e-785b-489d-9701-d77bc27e36f7.19.1"),sQuery(id+"F0.wireOp",EDGE,"261d038e-785b-489d-9701-d77bc27e36f7.19.2"),sQuery(id+"F0.wireOp",EDGE,"261d038e-785b-489d-9701-d77bc27e36f7.19.3"),sQuery(id+"F0.wireOp",EDGE,"261d038e-785b-489d-9701-d77bc27e36f7.19.4"),sQuery(id+"F0.wireOp",EDGE,"f45ad2ee-8b84-45a9-bb91-348b52f7b137.4.20.0"),sQuery(id+"F0.wireOp",EDGE,"f45ad2ee-8b84-45a9-bb91-348b52f7b137.8.20.0"),sQuery(id+"F0.wireOp",EDGE,"f45ad2ee-8b84-45a9-bb91-348b52f7b137.12.20.0"),sQuery(id+"F0.wireOp",EDGE,"f45ad2ee-8b84-45a9-bb91-348b52f7b137.15.20.0"),sQuery(id+"F0.wireOp",EDGE,"f45ad2ee-8b84-45a9-bb91-348b52f7b137.16.20.0")])],"isStart":true});
            var sketch = newSketch(context, id + "F4", { "sketchPlane" : qUnion([Q0])});
            skLineSegment(sketch, "E18", {"start": v(67.52, 0.69) * mm, "end": v(70.54, -9.37) * mm, "construction": true});
            skLineSegment(sketch, "E19", {"start": v(69.77, -9.54) * mm, "end": v(68.28, 0.85) * mm, "construction": true});
            skPoint(sketch, "E20", {"position": v(69.02, -4.33) * mm});
            skCircle(sketch, "E21", {"center": v(69.02, -4.33) * mm, "radius": 1.38 * mm});
            skSolve(sketch);
        }
        {
            var Q0;
            Q0=makeQuery(id+"F4.imprint","IMPRINT",FACE,{"disambiguationData":[TD([[makeQuery(id+"F4.imprint","IMPRINT",EDGE,{"derivedFrom":sQuery(id+"F4.wireOp",EDGE,"E21")}),1.0]])]});
            extrude(context, id + "F5", {"entities" : qUnion([Q0]), "operationType" : NewBodyOperationType.ADD, "depth" : (7 - 2.75) * mm});
        }
    });
